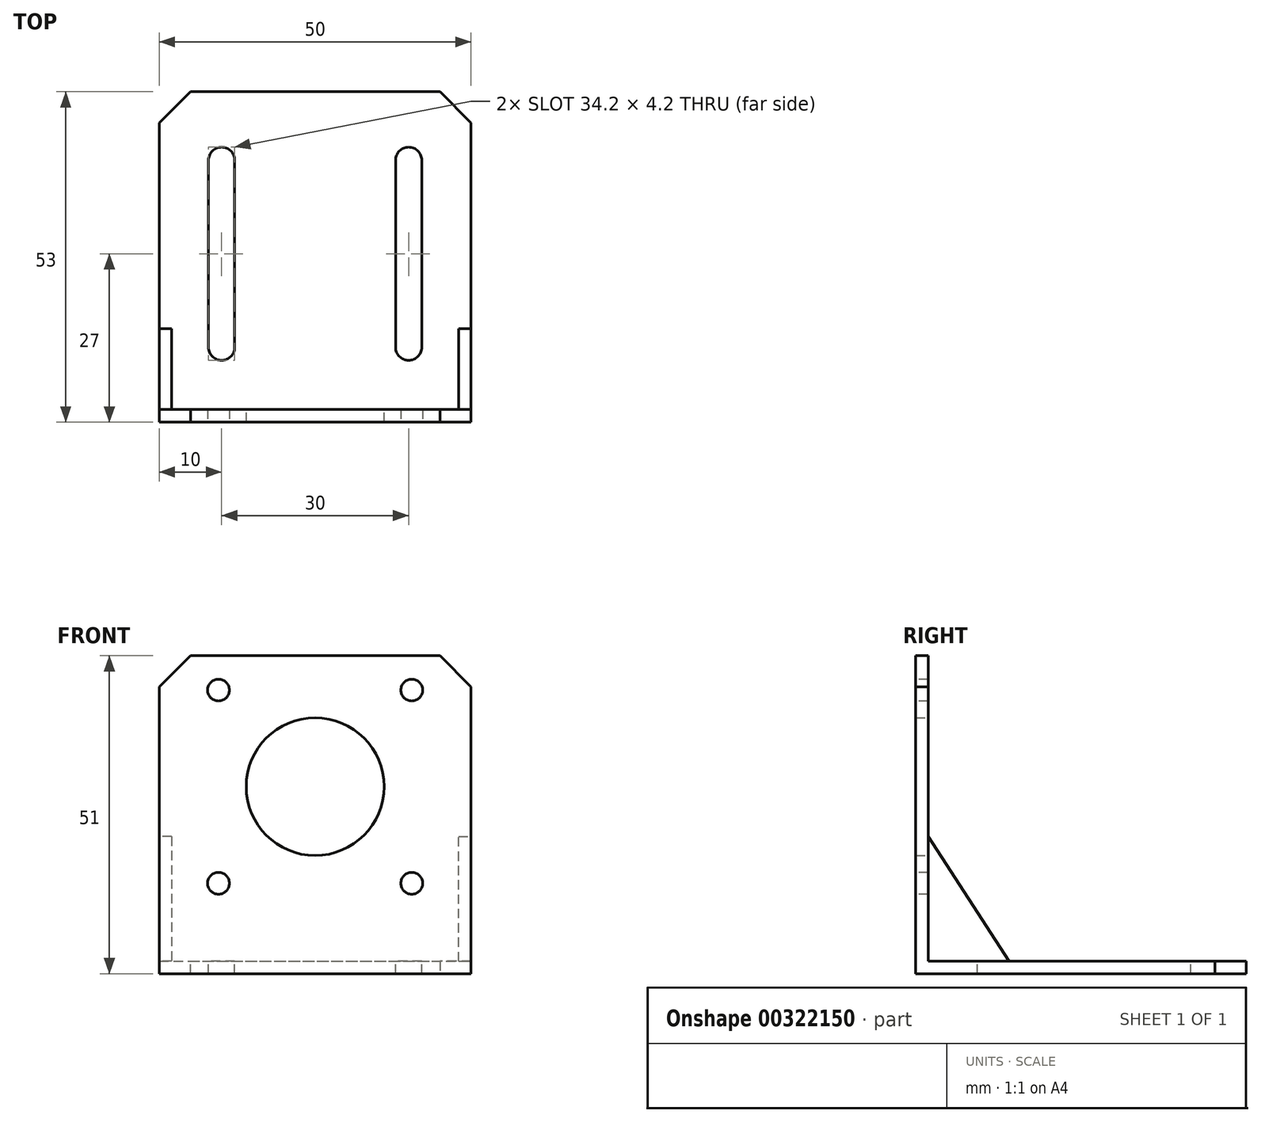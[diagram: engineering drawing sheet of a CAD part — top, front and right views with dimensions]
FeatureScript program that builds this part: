
annotation { "Feature Type Name" : "Feature", "Feature Type Description" : "" }
export const myFeature = defineFeature(function(context is Context, id is Id, definition is map)
    precondition{}
    {
        {
            var Q0;
            Q0=qCreatedBy(makeId("Right.planeOp"),FACE);
            var sketch = newSketch(context, id + "F0", { "sketchPlane" : qUnion([Q0])});
            skLineSegment(sketch, "E0", {"start": v(0, 51) * mm, "end": v(0, 0) * mm});
            skLineSegment(sketch, "E1", {"start": v(0, 0) * mm, "end": v(53, 0) * mm});
            skLineSegment(sketch, "E2.0", {"start": v(2, 2) * mm, "end": v(53, 2) * mm});
            skLineSegment(sketch, "E2.1", {"start": v(2, 51) * mm, "end": v(2, 2) * mm});
            skLineSegment(sketch, "E3", {"start": v(2, 51) * mm, "end": v(0, 51) * mm});
            skLineSegment(sketch, "E4", {"start": v(53, 2) * mm, "end": v(53, 0) * mm});
            skSolve(sketch);
        }
        {
            var Q0;
            Q0=makeQuery(id+"F0.imprint","IMPRINT",FACE,{"disambiguationData":[TD([[makeQuery(id+"F0.imprint","IMPRINT",EDGE,{"derivedFrom":sQuery(id+"F0.wireOp",EDGE,"E0")}),1.0]])]});
            extrude(context, id + "F1", {"entities" : qUnion([Q0]), "oppositeDirection" : true, "depth" : 50 * mm});
        }
        {
            var Q0;
            Q0=makeQuery(id+"F1.opExtrude","SWEPT_FACE",FACE,{"disambiguationData":[OSD([sQuery(id+"F0.wireOp",EDGE,"E2.1")])]});
            var sketch = newSketch(context, id + "F2", { "sketchPlane" : qUnion([Q0])});
            skCircle(sketch, "E5", {"center": v(25, 30) * mm, "radius": 11.05 * mm});
            skSolve(sketch);
        }
        {
            var Q0;
            Q0=makeQuery(id+"F2.imprint","IMPRINT",FACE,{"disambiguationData":[TD([[makeQuery(id+"F2.imprint","IMPRINT",EDGE,{"derivedFrom":sQuery(id+"F2.wireOp",EDGE,"E5")}),1.0]])]});
            extrude(context, id + "F3", {"entities" : qUnion([Q0]), "operationType" : NewBodyOperationType.REMOVE, "oppositeDirection" : true, "depth" : 2 * mm});
        }
        {
            var Q0;
            Q0=qCreatedBy(makeId("Front.planeOp"),FACE);
            var sketch = newSketch(context, id + "F4", { "sketchPlane" : qUnion([Q0])});
            skLineSegment(sketch, "E6", {"start": v(16.1, 30) * mm, "end": v(-68.79, 30) * mm, "construction": true});
            skLineSegment(sketch, "E7", {"start": v(-25, 58.5) * mm, "end": v(-25, -6.3) * mm, "construction": true});
            skPoint(sketch, "E8", {"position": v(-9.5, 45.5) * mm});
            skPoint(sketch, "E9", {"position": v(-40.5, 45.5) * mm});
            skPoint(sketch, "E10", {"position": v(-40.5, 14.5) * mm});
            skPoint(sketch, "E11", {"position": v(-9.5, 14.5) * mm});
            skSolve(sketch);
        }
        {
            var Q0;
            Q0=sQuery(id+"F4.wireOp",VERTEX,"E8");
            var Q1;
            Q1=sQuery(id+"F4.wireOp",VERTEX,"E9");
            var Q2;
            Q2=sQuery(id+"F4.wireOp",VERTEX,"E10");
            var Q3;
            Q3=sQuery(id+"F4.wireOp",VERTEX,"E11");
            var Q4;
            Q4=makeQuery(id+"F1.opExtrude","SWEPT_BODY",BODY,{"disambiguationData":[OSD([sQuery(id+"F0.wireOp",EDGE,"E0"),sQuery(id+"F0.wireOp",EDGE,"E1"),sQuery(id+"F0.wireOp",EDGE,"E2.0"),sQuery(id+"F0.wireOp",EDGE,"E2.1"),sQuery(id+"F0.wireOp",EDGE,"E3"),sQuery(id+"F0.wireOp",EDGE,"E4")])]});
            hole(context, id + "F5", {"style" : HoleStyle.SIMPLE, "endStyle" : HoleEndStyle.THROUGH, "holeDiameter" : 3.5 * mm, "tappedDepth" : 12 * mm, "tapClearance" : 3, "locations" : qUnion([Q0, Q1, Q2, Q3]), "scope" : qUnion([Q4])});
        }
        {
            var Q0;
            Q0=makeQuery(id+"F1.opExtrude","CAP_EDGE",EDGE,{"disambiguationData":[OSD([sQuery(id+"F0.wireOp",EDGE,"E3")])],"isStart":true});
            var Q1;
            Q1=makeQuery(id+"F1.opExtrude","CAP_EDGE",EDGE,{"disambiguationData":[OSD([sQuery(id+"F0.wireOp",EDGE,"E3")])],"isStart":false});
            chamfer(context, id + "F6", {"entities" : qUnion([Q0, Q1]), "width" : 5 * mm, "tangentPropagation" : true});
        }
        {
            var Q0;
            Q0=makeQuery(id+"F1.opExtrude","SWEPT_FACE",FACE,{"disambiguationData":[OSD([sQuery(id+"F0.wireOp",EDGE,"E2.0")])]});
            var sketch = newSketch(context, id + "F7", { "sketchPlane" : qUnion([Q0])});
            skLineSegment(sketch, "E12.left", {"start": v(-42.1, 42) * mm, "end": v(-42.1, 12) * mm});
            skLineSegment(sketch, "E12.right", {"start": v(-37.9, 42) * mm, "end": v(-37.9, 12) * mm});
            skLineSegment(sketch, "E13", {"start": v(-40, 56.38) * mm, "end": v(-40, -7.25) * mm, "construction": true});
            skArc(sketch, "E14", {"start": v(-37.9, 42) * mm, "mid": v(-40, 44.1) * mm, "end": v(-42.1, 42) * mm});
            skArc(sketch, "E15", {"start": v(-42.1, 12) * mm, "mid": v(-40, 9.9) * mm, "end": v(-37.9, 12) * mm});
            skArc(sketch, "E16.1.0.0", {"start": v(-12.1, 12) * mm, "mid": v(-10, 9.9) * mm, "end": v(-7.9, 12) * mm});
            skArc(sketch, "E16.1.0.1", {"start": v(-7.9, 42) * mm, "mid": v(-10, 44.1) * mm, "end": v(-12.1, 42) * mm});
            skLineSegment(sketch, "E16.1.0.2", {"start": v(-10, 56.38) * mm, "end": v(-10, -7.25) * mm, "construction": true});
            skLineSegment(sketch, "E16.1.0.3", {"start": v(-7.9, 42) * mm, "end": v(-7.9, 12) * mm});
            skLineSegment(sketch, "E16.1.0.4", {"start": v(-12.1, 42) * mm, "end": v(-12.1, 12) * mm});
            skLineSegment(sketch, "E16.direction1", {"start": v(-40, -7.25) * mm, "end": v(-10, -7.25) * mm, "construction": true});
            skSolve(sketch);
        }
        {
            var Q0;
            Q0=makeQuery(id+"F7.imprint","IMPRINT",FACE,{"disambiguationData":[TD([[makeQuery(id+"F7.imprint","IMPRINT",EDGE,{"derivedFrom":sQuery(id+"F7.wireOp",EDGE,"E16.1.0.0")}),1.0]])]});
            var Q1;
            Q1=makeQuery(id+"F7.imprint","IMPRINT",FACE,{"disambiguationData":[TD([[makeQuery(id+"F7.imprint","IMPRINT",EDGE,{"derivedFrom":sQuery(id+"F7.wireOp",EDGE,"E12.left")}),1.0]])]});
            extrude(context, id + "F8", {"entities" : qUnion([Q0, Q1]), "operationType" : NewBodyOperationType.REMOVE, "endBound" : BoundingType.UP_TO_NEXT, "oppositeDirection" : true, "depth" : 25 * mm});
        }
        {
            var Q0;
            Q0=makeQuery(id+"F1.opExtrude","CAP_EDGE",EDGE,{"disambiguationData":[OSD([sQuery(id+"F0.wireOp",EDGE,"E4")])],"isStart":false});
            chamfer(context, id + "F9", {"entities" : qUnion([Q0]), "width" : 5 * mm, "tangentPropagation" : true});
        }
        {
            var Q0;
            Q0=makeQuery(id+"F1.opExtrude","CAP_EDGE",EDGE,{"disambiguationData":[OSD([sQuery(id+"F0.wireOp",EDGE,"E4")])],"isStart":true});
            chamfer(context, id + "F10", {"entities" : qUnion([Q0]), "width" : 5 * mm, "tangentPropagation" : true});
        }
        {
            var Q0;
            Q0=makeQuery(id+"F1.opExtrude","CAP_FACE",FACE,{"disambiguationData":[OSD([sQuery(id+"F0.wireOp",EDGE,"E0"),sQuery(id+"F0.wireOp",EDGE,"E1"),sQuery(id+"F0.wireOp",EDGE,"E2.0"),sQuery(id+"F0.wireOp",EDGE,"E2.1"),sQuery(id+"F0.wireOp",EDGE,"E3"),sQuery(id+"F0.wireOp",EDGE,"E4")])],"isStart":true});
            var sketch = newSketch(context, id + "F11", { "sketchPlane" : qUnion([Q0])});
            skLineSegment(sketch, "E17", {"start": v(2, 2) * mm, "end": v(15, 2) * mm});
            skLineSegment(sketch, "E18", {"start": v(15, 2) * mm, "end": v(2, 22) * mm});
            skLineSegment(sketch, "E19", {"start": v(2, 22) * mm, "end": v(2, 2) * mm});
            skSolve(sketch);
        }
        {
            var Q0;
            Q0=makeQuery(id+"F11.imprint","IMPRINT",FACE,{"disambiguationData":[TD([[makeQuery(id+"F11.imprint","IMPRINT",EDGE,{"derivedFrom":sQuery(id+"F11.wireOp",EDGE,"E17")}),1.0]])]});
            extrude(context, id + "F12", {"entities" : qUnion([Q0]), "oppositeDirection" : true, "depth" : 2 * mm});
        }
        {
            var Q0;
            Q0=makeQuery(id+"F1.opExtrude","CAP_FACE",FACE,{"disambiguationData":[OSD([sQuery(id+"F0.wireOp",EDGE,"E0"),sQuery(id+"F0.wireOp",EDGE,"E1"),sQuery(id+"F0.wireOp",EDGE,"E2.0"),sQuery(id+"F0.wireOp",EDGE,"E2.1"),sQuery(id+"F0.wireOp",EDGE,"E3"),sQuery(id+"F0.wireOp",EDGE,"E4")])],"isStart":false});
            var sketch = newSketch(context, id + "F13", { "sketchPlane" : qUnion([Q0])});
            skLineSegment(sketch, "E20", {"start": v(-2, 2) * mm, "end": v(-15, 2) * mm});
            skLineSegment(sketch, "E21", {"start": v(-2, 2) * mm, "end": v(-2, 22) * mm});
            skLineSegment(sketch, "E22", {"start": v(-2, 22) * mm, "end": v(-15, 2) * mm});
            skSolve(sketch);
        }
        {
            var Q0;
            Q0 = qSketchRegion(id + "F13", true);
            extrude(context, id + "F14", {"entities" : qUnion([Q0]), "oppositeDirection" : true, "depth" : 2 * mm});
        }
    });
